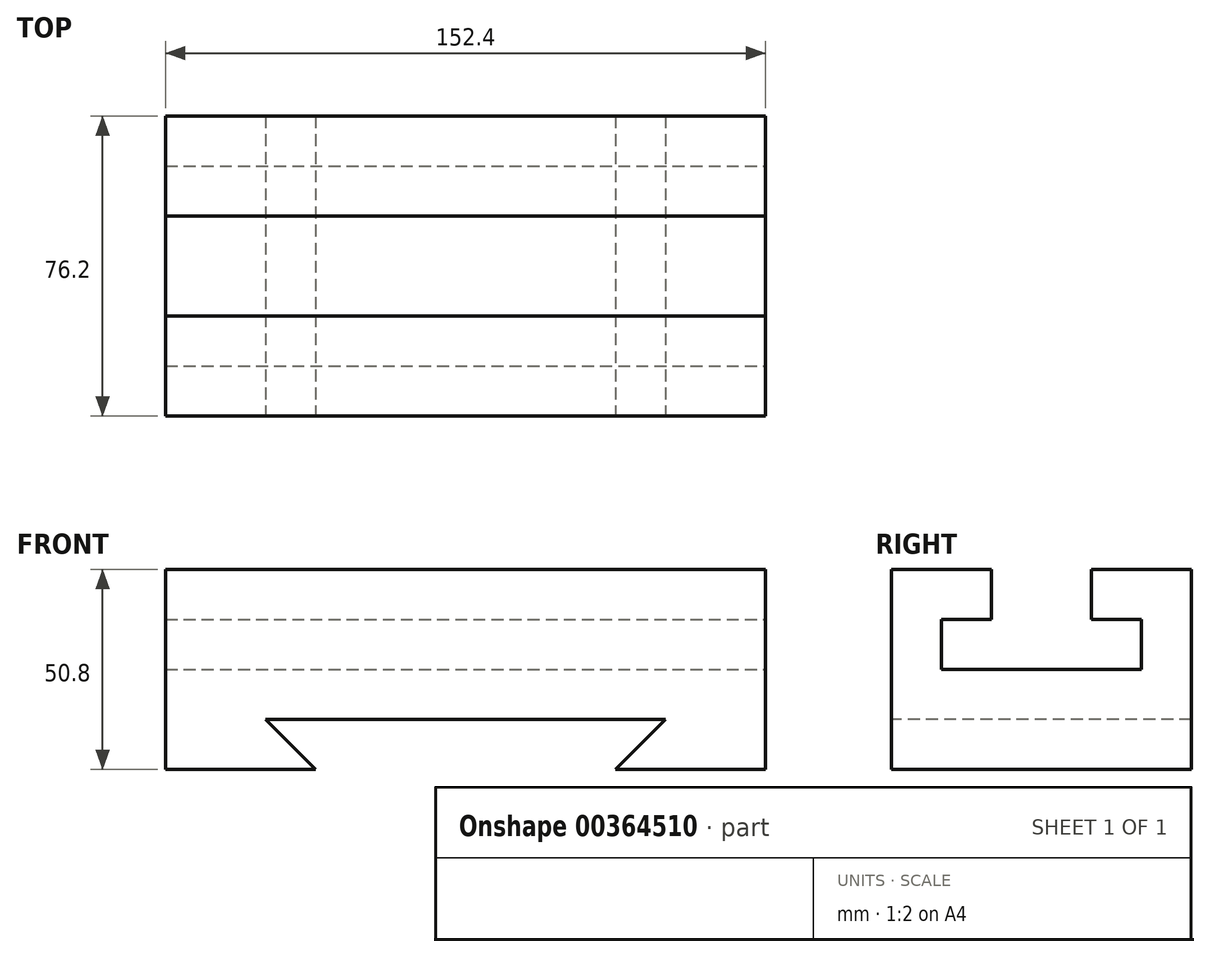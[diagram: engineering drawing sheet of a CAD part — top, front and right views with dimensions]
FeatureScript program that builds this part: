
annotation { "Feature Type Name" : "Feature", "Feature Type Description" : "" }
export const myFeature = defineFeature(function(context is Context, id is Id, definition is map)
    precondition{}
    {
        {
            var Q0;
            Q0=qCreatedBy(makeId("Top.planeOp"),FACE);
            var sketch = newSketch(context, id + "F0", { "sketchPlane" : qUnion([Q0])});
            skLineSegment(sketch, "E0.bottom", {"start": v(-76.2, 38.1) * mm, "end": v(76.2, 38.1) * mm});
            skLineSegment(sketch, "E0.top", {"start": v(-76.2, -38.1) * mm, "end": v(76.2, -38.1) * mm});
            skLineSegment(sketch, "E0.left", {"start": v(-76.2, 38.1) * mm, "end": v(-76.2, -38.1) * mm});
            skLineSegment(sketch, "E0.right", {"start": v(76.2, 38.1) * mm, "end": v(76.2, -38.1) * mm});
            skPoint(sketch, "E0.middle", {"position": v(0, 0) * mm});
            skSolve(sketch);
        }
        {
            var Q0;
            Q0=qSketchRegion(id+"F0",true);
            extrude(context, id + "F1", {"entities" : qUnion([Q0]), "depth" : 50.8 * mm});
        }
        {
            var Q0;
            Q0=makeQuery(id+"F1.opExtrude","SWEPT_FACE",FACE,{"disambiguationData":[OSD([sQuery(id+"F0.wireOp",EDGE,"E0.top")])]});
            var sketch = newSketch(context, id + "F2", { "sketchPlane" : qUnion([Q0])});
            skLineSegment(sketch, "E1", {"start": v(-76.2, 0) * mm, "end": v(-38.1, 0) * mm});
            skLineSegment(sketch, "E2", {"start": v(76.2, 0) * mm, "end": v(38.1, 0) * mm});
            skLineSegment(sketch, "E3", {"start": v(-76.2, 0) * mm, "end": v(-50.8, 0) * mm});
            skLineSegment(sketch, "E4", {"start": v(76.2, 0) * mm, "end": v(50.8, 0) * mm});
            skLineSegment(sketch, "E5", {"start": v(-50.8, 0) * mm, "end": v(-50.8, 12.7) * mm});
            skLineSegment(sketch, "E6", {"start": v(50.8, 0) * mm, "end": v(50.8, 12.7) * mm});
            skLineSegment(sketch, "E7", {"start": v(-38.1, 0) * mm, "end": v(38.1, 0) * mm});
            skLineSegment(sketch, "E8", {"start": v(-50.8, 12.7) * mm, "end": v(50.8, 12.7) * mm});
            skLineSegment(sketch, "E9", {"start": v(-50.8, 12.7) * mm, "end": v(-38.1, 0) * mm});
            skLineSegment(sketch, "E10", {"start": v(38.1, 0) * mm, "end": v(50.8, 12.7) * mm});
            skSolve(sketch);
        }
        {
            var Q0;
            Q0=makeQuery(id+"F2.imprint","IMPRINT",FACE,{"disambiguationData":[TD([[makeQuery(id+"F2.imprint","IMPRINT",EDGE,{"derivedFrom":sQuery(id+"F2.wireOp",EDGE,"E7")}),1.0]])]});
            extrude(context, id + "F3", {"entities" : qUnion([Q0]), "operationType" : NewBodyOperationType.REMOVE, "endBound" : BoundingType.THROUGH_ALL, "oppositeDirection" : true, "depth" : 25.4 * mm});
        }
        {
            var Q0;
            Q0=makeQuery(id+"F1.opExtrude","SWEPT_FACE",FACE,{"disambiguationData":[OSD([sQuery(id+"F0.wireOp",EDGE,"E0.right")])]});
            var sketch = newSketch(context, id + "F4", { "sketchPlane" : qUnion([Q0])});
            skLineSegment(sketch, "E11", {"start": v(-38.1, 50.8) * mm, "end": v(-12.7, 50.8) * mm});
            skLineSegment(sketch, "E12", {"start": v(38.1, 50.8) * mm, "end": v(12.7, 50.8) * mm});
            skLineSegment(sketch, "E13", {"start": v(-12.7, 50.8) * mm, "end": v(-12.7, 38.1) * mm});
            skLineSegment(sketch, "E14", {"start": v(12.7, 50.8) * mm, "end": v(12.7, 38.1) * mm});
            skLineSegment(sketch, "E15", {"start": v(-12.7, 38.1) * mm, "end": v(-25.4, 38.1) * mm});
            skLineSegment(sketch, "E16", {"start": v(12.7, 38.1) * mm, "end": v(25.4, 38.1) * mm});
            skLineSegment(sketch, "E17", {"start": v(-25.4, 38.1) * mm, "end": v(-25.4, 25.4) * mm});
            skLineSegment(sketch, "E18", {"start": v(-25.4, 25.4) * mm, "end": v(25.4, 25.4) * mm});
            skLineSegment(sketch, "E19", {"start": v(25.4, 25.4) * mm, "end": v(25.4, 38.1) * mm});
            skSolve(sketch);
        }
        {
            var Q0;
            {var subQ1=sQuery(id+"F4.wireOp",EDGE,"E13");Q0=makeQuery(id+"F4.imprint","IMPRINT",FACE,{"disambiguationData":[TD([[makeQuery(id+"F4.imprint","IMPRINT",EDGE,{"derivedFrom":subQ1}),1.0]])]});}
            extrude(context, id + "F5", {"entities" : qUnion([Q0]), "operationType" : NewBodyOperationType.REMOVE, "endBound" : BoundingType.THROUGH_ALL, "oppositeDirection" : true, "depth" : 25.4 * mm});
        }
    });
